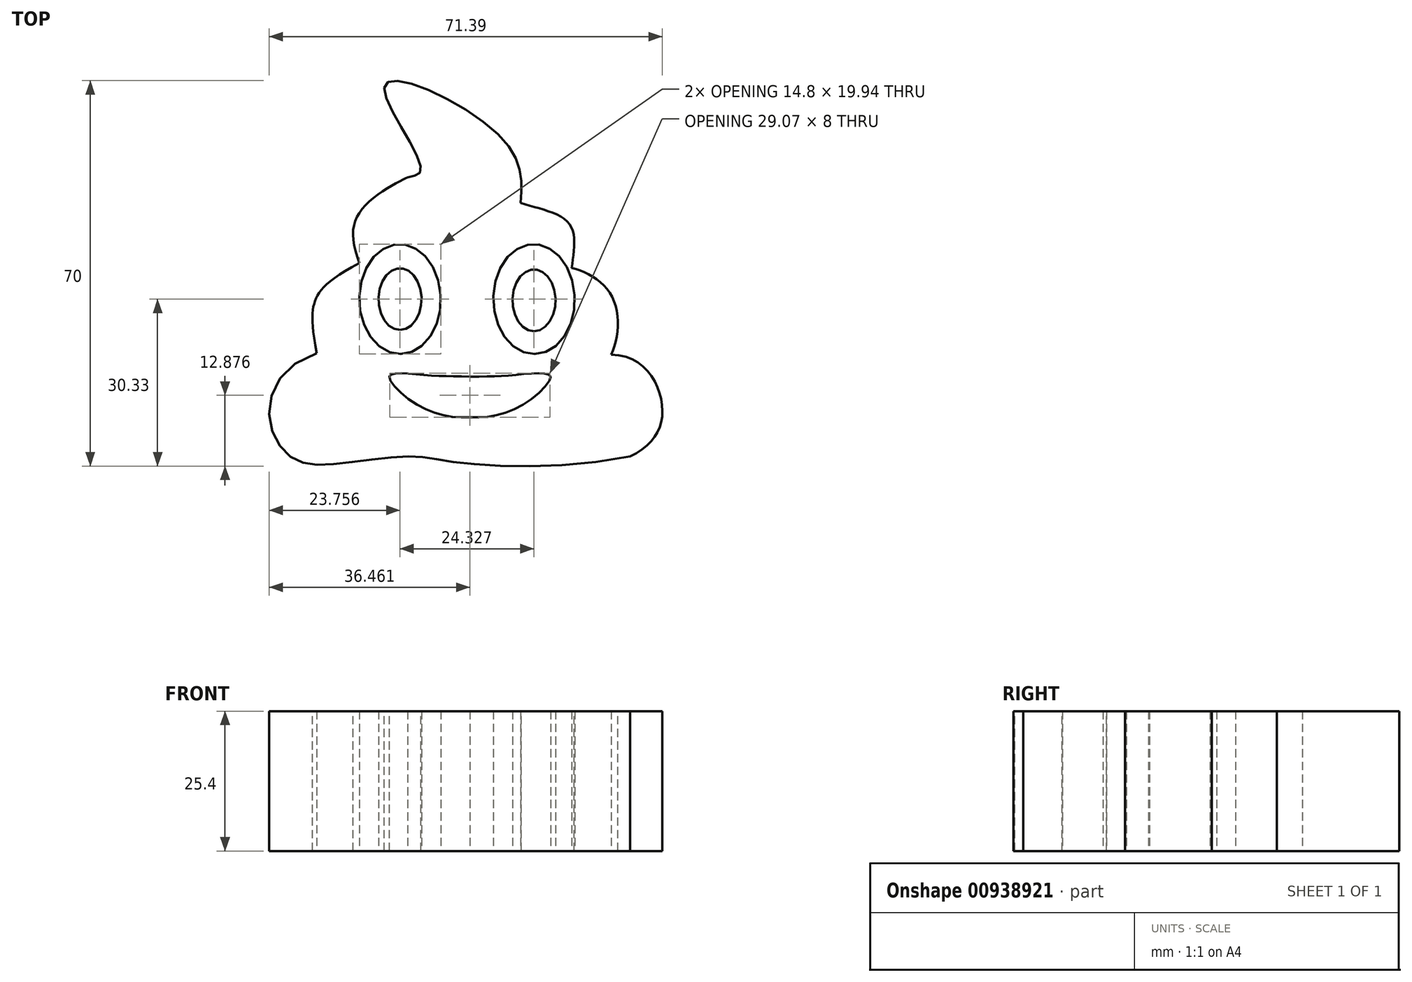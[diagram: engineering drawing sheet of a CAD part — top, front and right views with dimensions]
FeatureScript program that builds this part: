
annotation { "Feature Type Name" : "Feature", "Feature Type Description" : "" }
export const myFeature = defineFeature(function(context is Context, id is Id, definition is map)
    precondition{}
    {
        {
            var Q0;
            Q0=qCreatedBy(makeId("Top.planeOp"),FACE);
            var sketch = newSketch(context, id + "F0", { "sketchPlane" : qUnion([Q0])});
            skFitSpline(sketch, "E0", {"points": [v(9.18, 16.32) * mm, v(18.11, 12.4) * mm, v(18.48, 4.52) * mm], "startDerivative": vector(18.51, -5.94) * mm, "endDerivative": vector(-1.92, -16.81) * mm});
            skFitSpline(sketch, "E1", {"points": [v(18.48, 4.52) * mm, v(25.87, -0.9) * mm, v(25.63, -11.25) * mm], "startDerivative": vector(17.1, -4.27) * mm, "endDerivative": vector(-7.9, -16.5) * mm});
            skFitSpline(sketch, "E2", {"points": [v(25.63, -11.25) * mm, v(34.87, -20.36) * mm, v(29.08, -29.73) * mm], "startDerivative": vector(33.14, 0) * mm, "endDerivative": vector(-28, -12.86) * mm});
            skFitSpline(sketch, "E3", {"points": [v(29.08, -29.73) * mm, v(-3.08, -30.71) * mm, v(-11.33, -29.73) * mm, v(-24.39, -31.08) * mm, v(-32.27, -29.97) * mm, v(-36.46, -21.84) * mm, v(-27.84, -11) * mm], "startDerivative": vector(-143.22, -28.36) * mm, "endDerivative": vector(105.02, 30.63) * mm});
            skFitSpline(sketch, "E4", {"points": [v(-27.84, -11) * mm, v(-28.08, -1.4) * mm, v(-20.08, 5.38) * mm], "startDerivative": vector(-6.24, 35.12) * mm, "endDerivative": vector(33.7, 17.55) * mm});
            skFitSpline(sketch, "E5", {"points": [v(-20.08, 5.38) * mm, v(-19.13, 15.75) * mm, v(-11.3, 20.98) * mm], "startDerivative": vector(-10.3, 27.23) * mm, "endDerivative": vector(6.22, 2.7) * mm});
            skEllipse(sketch, "E6", {"center": v(-12.7, -1.16) * mm, "majorRadius": 9.97 * mm, "minorRadius": 7.4 * mm, "majorAxis": v(0.01, -1)});
            skEllipse(sketch, "E7", {"center": v(11.62, -1.16) * mm, "majorRadius": 9.97 * mm, "minorRadius": 7.4 * mm, "majorAxis": v(0.01, -1)});
            skEllipse(sketch, "E8", {"center": v(-12.7, -1.16) * mm, "majorRadius": 5.6 * mm, "minorRadius": 3.9 * mm, "majorAxis": v(0, -1)});
            skEllipse(sketch, "E9", {"center": v(11.62, -1.4) * mm, "majorRadius": 5.6 * mm, "minorRadius": 3.9 * mm, "majorAxis": v(0, -1)});
            skFitSpline(sketch, "E10", {"points": [v(0, -15.21) * mm, v(-6.91, -15.04) * mm, v(-13.21, -14.62) * mm, v(-14.64, -15.3) * mm, v(-9.32, -20.5) * mm, v(0.04, -22.61) * mm], "startDerivative": vector(-37.78, 1.22) * mm, "endDerivative": vector(37.28, 2.11) * mm});
            skFitSpline(sketch, "E11.MirrorCS", {"points": [v(0, -15.21) * mm, v(6.91, -15.04) * mm, v(13.21, -14.62) * mm, v(14.64, -15.3) * mm, v(9.32, -20.5) * mm, v(-0.04, -22.61) * mm], "startDerivative": vector(41.6, -0.18) * mm, "endDerivative": vector(-37.28, 2.11) * mm});
            skFitSpline(sketch, "E12", {"points": [v(-11.3, 20.98) * mm, v(-8.9, 22.7) * mm, v(-15.4, 37.77) * mm, v(5.6, 28.29) * mm, v(9.18, 16.32) * mm], "startDerivative": vector(30.6, 4.77) * mm, "endDerivative": vector(-3.54, -45.98) * mm});
            skSolve(sketch);
        }
        {
            var Q0;
            Q0=makeQuery(id+"F0.imprint","IMPRINT",FACE,{"disambiguationData":[TD([[makeQuery(id+"F0.imprint","IMPRINT",EDGE,{"derivedFrom":sQuery(id+"F0.wireOp",EDGE,"02d3c3e2-d45b-4835-a2a2-d94a3edcca88")}),-1.0]])]});
            var Q1;
            Q1=makeQuery(id+"F0.imprint","IMPRINT",FACE,{"disambiguationData":[TD([[makeQuery(id+"F0.imprint","IMPRINT",EDGE,{"derivedFrom":sQuery(id+"F0.wireOp",EDGE,"E8")}),1.0]])]});
            var Q2;
            Q2=makeQuery(id+"F0.imprint","IMPRINT",FACE,{"disambiguationData":[TD([[makeQuery(id+"F0.imprint","IMPRINT",EDGE,{"derivedFrom":sQuery(id+"F0.wireOp",EDGE,"E9")}),1.0]])]});
            var Q3;
            Q3=makeQuery(id+"F0.imprint","IMPRINT",FACE,{"disambiguationData":[TD([[makeQuery(id+"F0.imprint","IMPRINT",EDGE,{"derivedFrom":sQuery(id+"F0.wireOp",EDGE,"E0")}),-1.0]])]});
            extrude(context, id + "F1", {"entities" : qUnion([Q0, Q1, Q2, Q3]), "depth" : 25.4 * mm, "offsetDistance" : 25.4 * mm});
        }
    });
